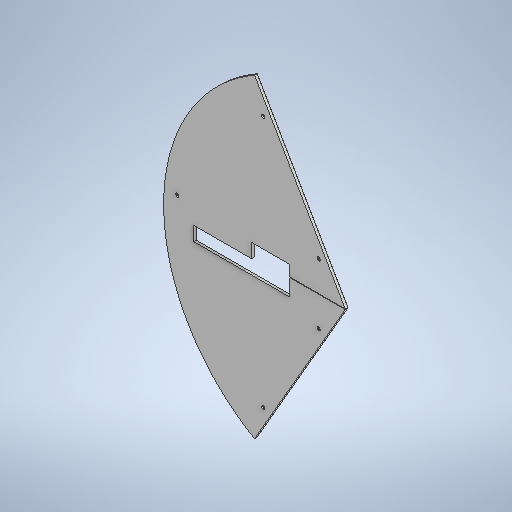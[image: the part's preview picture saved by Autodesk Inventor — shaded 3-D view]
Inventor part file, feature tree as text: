
AUTODESK INVENTOR PART (.ipt)
format: ipt  version: 2025.1 (Build 291241000, 241)  size: 318,976 bytes
history: native  units: mm
features: extrude x4, sketch x4, fillet x2, chamfer x1
ambient origin geometry x8: Origin, YZ Plane, XZ Plane, XY Plane, X Axis, Y Axis, Z Axis, Center Point
bodies: Volumenkörper1 (feature_tree)
feature tree (11):
  extrude  "Extrusion1"  TaperAngle=120.0deg  [1 undecoded]
  fillet  "Rundung1"  [1 undecoded]
  extrude  "Extrusion2"  Depth=0.5mm
  fillet  "Rundung2"  Radius=14.0mm
  extrude  "Extrusion3"  Depth=17.0mm
  extrude  "Extrusion4"  Depth=3.0mm TaperAngle=0.0deg
  chamfer  "Fasen1"  Distance=38.0mm
  sketch  "Skizze1"  dims[d0=360.0mm d1=120.0deg d2=60.0deg]
  sketch  "Skizze2"  dims[d3=3.0mm d4=0.0mm d5=0.5mm d6=14.0mm]
  sketch  "Skizze3"  dims[d7=95.0mm d8=17.0mm]
  sketch  "Skizze4"  dims[d10=150.0mm d11=3.0mm d12=0.0mm d13=38.0mm d14=14.0mm d15=0.5mm d16=0.5mm d17=0.25mm d18=60.0mm d19=0.0mm d20=3.0mm d21=0.0mm d26=26.558mm d27=26.558mm d28=3.3mm d29=81.406mm d30=81.406mm d31=14.8mm d32=166.5mm d33=125.0mm d34=30.0mm d35=30.0mm d36=125.0mm d37=3.0mm d38=0.0mm d39=1.9mm d40=2.0mm d41=45.0deg]
note: 2 required parameter values undecoded (feature->parameter linkage not recoverable at this tier; creation-order binding heuristic only, values carry confidence <= 0.55)
